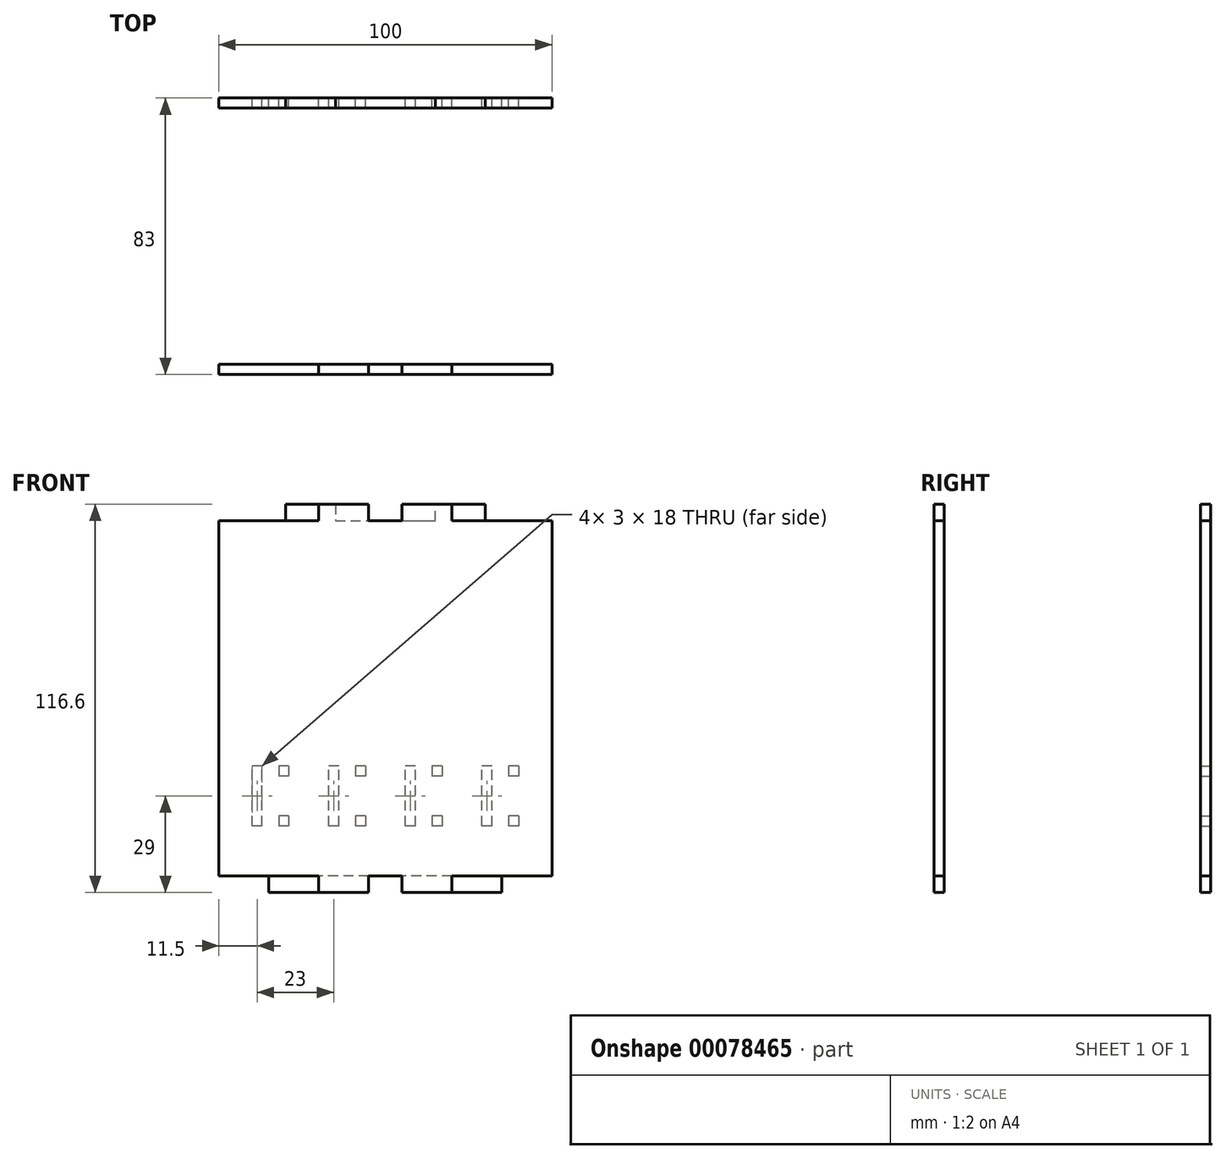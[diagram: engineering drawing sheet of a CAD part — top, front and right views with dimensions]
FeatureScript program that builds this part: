
annotation { "Feature Type Name" : "Feature", "Feature Type Description" : "" }
export const myFeature = defineFeature(function(context is Context, id is Id, definition is map)
    precondition{}
    {
        {
            var Q0;
            Q0=qCreatedBy(makeId("Front.planeOp"),FACE);
            var sketch = newSketch(context, id + "F0", { "sketchPlane" : qUnion([Q0])});
            skLineSegment(sketch, "E0", {"start": v(-50, 53.3) * mm, "end": v(-30, 53.3) * mm});
            skLineSegment(sketch, "E1", {"start": v(-30, 53.3) * mm, "end": v(-30, 58.3) * mm});
            skLineSegment(sketch, "E2", {"start": v(-30, 58.3) * mm, "end": v(-15, 58.3) * mm});
            skLineSegment(sketch, "E3", {"start": v(-15, 58.3) * mm, "end": v(-15, 53.3) * mm});
            skLineSegment(sketch, "E4", {"start": v(-15, 53.3) * mm, "end": v(15, 53.3) * mm});
            skLineSegment(sketch, "E5", {"start": v(15, 53.3) * mm, "end": v(15, 58.3) * mm});
            skLineSegment(sketch, "E6", {"start": v(15, 58.3) * mm, "end": v(30, 58.3) * mm});
            skLineSegment(sketch, "E7", {"start": v(30, 58.3) * mm, "end": v(30, 53.3) * mm});
            skLineSegment(sketch, "E8", {"start": v(30, 53.3) * mm, "end": v(50, 53.3) * mm});
            skLineSegment(sketch, "E9", {"start": v(50, 53.3) * mm, "end": v(50, -53.3) * mm});
            skLineSegment(sketch, "E10", {"start": v(50, -53.3) * mm, "end": v(35, -53.3) * mm});
            skLineSegment(sketch, "E11", {"start": v(35, -53.3) * mm, "end": v(35, -58.3) * mm});
            skLineSegment(sketch, "E12", {"start": v(35, -58.3) * mm, "end": v(20, -58.3) * mm});
            skLineSegment(sketch, "E13", {"start": v(20, -58.3) * mm, "end": v(20, -53.3) * mm});
            skLineSegment(sketch, "E14", {"start": v(20, -53.3) * mm, "end": v(-20, -53.3) * mm});
            skLineSegment(sketch, "E15", {"start": v(-20, -53.3) * mm, "end": v(-20, -58.3) * mm});
            skLineSegment(sketch, "E16", {"start": v(-20, -58.3) * mm, "end": v(-35, -58.3) * mm});
            skLineSegment(sketch, "E17", {"start": v(-35, -58.3) * mm, "end": v(-35, -53.3) * mm});
            skLineSegment(sketch, "E18", {"start": v(-35, -53.3) * mm, "end": v(-50, -53.3) * mm});
            skLineSegment(sketch, "E19", {"start": v(-50, -53.3) * mm, "end": v(-50, 53.3) * mm});
            skPoint(sketch, "E20", {"position": v(-50, 0) * mm});
            skLineSegment(sketch, "E21", {"start": v(-50, 0) * mm, "end": v(50, 0) * mm, "construction": true});
            skPoint(sketch, "E22", {"position": v(0, 0) * mm});
            skLineSegment(sketch, "E23.bottom", {"start": v(40, -20.3) * mm, "end": v(37, -20.3) * mm});
            skLineSegment(sketch, "E23.top", {"start": v(40, -23.3) * mm, "end": v(37, -23.3) * mm});
            skLineSegment(sketch, "E23.left", {"start": v(40, -20.3) * mm, "end": v(40, -23.3) * mm});
            skLineSegment(sketch, "E23.right", {"start": v(37, -20.3) * mm, "end": v(37, -23.3) * mm});
            skLineSegment(sketch, "E24.0.1.0", {"start": v(37, -35.3) * mm, "end": v(37, -38.3) * mm});
            skLineSegment(sketch, "E24.0.1.1", {"start": v(40, -35.3) * mm, "end": v(40, -38.3) * mm});
            skLineSegment(sketch, "E24.0.1.2", {"start": v(40, -38.3) * mm, "end": v(37, -38.3) * mm});
            skLineSegment(sketch, "E24.0.1.3", {"start": v(40, -35.3) * mm, "end": v(37, -35.3) * mm});
            skLineSegment(sketch, "E24.direction2", {"start": v(37, -23.3) * mm, "end": v(37, -38.3) * mm, "construction": true});
            skLineSegment(sketch, "E25.0.3.0", {"start": v(-194, -20.3) * mm, "end": v(-194, -23.3) * mm});
            skLineSegment(sketch, "E25.3.3.0", {"start": v(-191, -20.3) * mm, "end": v(-191, -23.3) * mm});
            skLineSegment(sketch, "E25.6.3.0", {"start": v(-191, -23.3) * mm, "end": v(-194, -23.3) * mm});
            skLineSegment(sketch, "E25.9.3.0", {"start": v(-191, -20.3) * mm, "end": v(-194, -20.3) * mm});
            skLineSegment(sketch, "E25.0.3.1", {"start": v(-194, -35.3) * mm, "end": v(-194, -38.3) * mm});
            skLineSegment(sketch, "E25.3.3.1", {"start": v(-191, -35.3) * mm, "end": v(-191, -38.3) * mm});
            skLineSegment(sketch, "E25.6.3.1", {"start": v(-191, -38.3) * mm, "end": v(-194, -38.3) * mm});
            skLineSegment(sketch, "E25.9.3.1", {"start": v(-191, -35.3) * mm, "end": v(-194, -35.3) * mm});
            skLineSegment(sketch, "E25.0.4.0", {"start": v(-271, -20.3) * mm, "end": v(-271, -23.3) * mm});
            skLineSegment(sketch, "E25.3.4.0", {"start": v(-268, -20.3) * mm, "end": v(-268, -23.3) * mm});
            skLineSegment(sketch, "E25.6.4.0", {"start": v(-268, -23.3) * mm, "end": v(-271, -23.3) * mm});
            skLineSegment(sketch, "E25.9.4.0", {"start": v(-268, -20.3) * mm, "end": v(-271, -20.3) * mm});
            skLineSegment(sketch, "E25.0.4.1", {"start": v(-271, -35.3) * mm, "end": v(-271, -38.3) * mm});
            skLineSegment(sketch, "E25.3.4.1", {"start": v(-268, -35.3) * mm, "end": v(-268, -38.3) * mm});
            skLineSegment(sketch, "E25.6.4.1", {"start": v(-268, -38.3) * mm, "end": v(-271, -38.3) * mm});
            skLineSegment(sketch, "E25.9.4.1", {"start": v(-268, -35.3) * mm, "end": v(-271, -35.3) * mm});
            skLineSegment(sketch, "E25.0.5.0", {"start": v(-348, -20.3) * mm, "end": v(-348, -23.3) * mm});
            skLineSegment(sketch, "E25.3.5.0", {"start": v(-345, -20.3) * mm, "end": v(-345, -23.3) * mm});
            skLineSegment(sketch, "E25.6.5.0", {"start": v(-345, -23.3) * mm, "end": v(-348, -23.3) * mm});
            skLineSegment(sketch, "E25.9.5.0", {"start": v(-345, -20.3) * mm, "end": v(-348, -20.3) * mm});
            skLineSegment(sketch, "E25.0.5.1", {"start": v(-348, -35.3) * mm, "end": v(-348, -38.3) * mm});
            skLineSegment(sketch, "E25.3.5.1", {"start": v(-345, -35.3) * mm, "end": v(-345, -38.3) * mm});
            skLineSegment(sketch, "E25.6.5.1", {"start": v(-345, -38.3) * mm, "end": v(-348, -38.3) * mm});
            skLineSegment(sketch, "E25.9.5.1", {"start": v(-345, -35.3) * mm, "end": v(-348, -35.3) * mm});
            skLineSegment(sketch, "E26.bottom", {"start": v(32, -38.3) * mm, "end": v(29, -38.3) * mm});
            skLineSegment(sketch, "E26.top", {"start": v(32, -20.3) * mm, "end": v(29, -20.3) * mm});
            skLineSegment(sketch, "E26.left", {"start": v(32, -38.3) * mm, "end": v(32, -20.3) * mm});
            skLineSegment(sketch, "E26.right", {"start": v(29, -38.3) * mm, "end": v(29, -20.3) * mm});
            skLineSegment(sketch, "E27.1.0.0", {"start": v(14, -23.3) * mm, "end": v(14, -38.3) * mm, "construction": true});
            skLineSegment(sketch, "E27.1.0.1", {"start": v(9, -38.3) * mm, "end": v(9, -20.3) * mm});
            skLineSegment(sketch, "E27.1.0.2", {"start": v(6, -38.3) * mm, "end": v(6, -20.3) * mm});
            skLineSegment(sketch, "E27.1.0.3", {"start": v(17, -35.3) * mm, "end": v(17, -38.3) * mm});
            skLineSegment(sketch, "E27.1.0.4", {"start": v(14, -35.3) * mm, "end": v(14, -38.3) * mm});
            skLineSegment(sketch, "E27.1.0.5", {"start": v(17, -35.3) * mm, "end": v(14, -35.3) * mm});
            skLineSegment(sketch, "E27.1.0.6", {"start": v(17, -20.3) * mm, "end": v(17, -23.3) * mm});
            skLineSegment(sketch, "E27.1.0.7", {"start": v(17, -38.3) * mm, "end": v(14, -38.3) * mm});
            skLineSegment(sketch, "E27.1.0.8", {"start": v(14, -20.3) * mm, "end": v(14, -23.3) * mm});
            skLineSegment(sketch, "E27.1.0.9", {"start": v(9, -20.3) * mm, "end": v(6, -20.3) * mm});
            skLineSegment(sketch, "E27.1.0.10", {"start": v(9, -38.3) * mm, "end": v(6, -38.3) * mm});
            skLineSegment(sketch, "E27.1.0.11", {"start": v(17, -23.3) * mm, "end": v(14, -23.3) * mm});
            skLineSegment(sketch, "E27.1.0.12", {"start": v(17, -20.3) * mm, "end": v(14, -20.3) * mm});
            skLineSegment(sketch, "E27.2.0.0", {"start": v(-9, -23.3) * mm, "end": v(-9, -38.3) * mm, "construction": true});
            skLineSegment(sketch, "E27.2.0.1", {"start": v(-14, -38.3) * mm, "end": v(-14, -20.3) * mm});
            skLineSegment(sketch, "E27.2.0.2", {"start": v(-17, -38.3) * mm, "end": v(-17, -20.3) * mm});
            skLineSegment(sketch, "E27.2.0.3", {"start": v(-6, -35.3) * mm, "end": v(-6, -38.3) * mm});
            skLineSegment(sketch, "E27.2.0.4", {"start": v(-9, -35.3) * mm, "end": v(-9, -38.3) * mm});
            skLineSegment(sketch, "E27.2.0.5", {"start": v(-6, -35.3) * mm, "end": v(-9, -35.3) * mm});
            skLineSegment(sketch, "E27.2.0.6", {"start": v(-6, -20.3) * mm, "end": v(-6, -23.3) * mm});
            skLineSegment(sketch, "E27.2.0.7", {"start": v(-6, -38.3) * mm, "end": v(-9, -38.3) * mm});
            skLineSegment(sketch, "E27.2.0.8", {"start": v(-9, -20.3) * mm, "end": v(-9, -23.3) * mm});
            skLineSegment(sketch, "E27.2.0.9", {"start": v(-14, -20.3) * mm, "end": v(-17, -20.3) * mm});
            skLineSegment(sketch, "E27.2.0.10", {"start": v(-14, -38.3) * mm, "end": v(-17, -38.3) * mm});
            skLineSegment(sketch, "E27.2.0.11", {"start": v(-6, -23.3) * mm, "end": v(-9, -23.3) * mm});
            skLineSegment(sketch, "E27.2.0.12", {"start": v(-6, -20.3) * mm, "end": v(-9, -20.3) * mm});
            skLineSegment(sketch, "E27.3.0.0", {"start": v(-32, -23.3) * mm, "end": v(-32, -38.3) * mm, "construction": true});
            skLineSegment(sketch, "E27.3.0.1", {"start": v(-37, -38.3) * mm, "end": v(-37, -20.3) * mm});
            skLineSegment(sketch, "E27.3.0.2", {"start": v(-40, -38.3) * mm, "end": v(-40, -20.3) * mm});
            skLineSegment(sketch, "E27.3.0.3", {"start": v(-29, -35.3) * mm, "end": v(-29, -38.3) * mm});
            skLineSegment(sketch, "E27.3.0.4", {"start": v(-32, -35.3) * mm, "end": v(-32, -38.3) * mm});
            skLineSegment(sketch, "E27.3.0.5", {"start": v(-29, -35.3) * mm, "end": v(-32, -35.3) * mm});
            skLineSegment(sketch, "E27.3.0.6", {"start": v(-29, -20.3) * mm, "end": v(-29, -23.3) * mm});
            skLineSegment(sketch, "E27.3.0.7", {"start": v(-29, -38.3) * mm, "end": v(-32, -38.3) * mm});
            skLineSegment(sketch, "E27.3.0.8", {"start": v(-32, -20.3) * mm, "end": v(-32, -23.3) * mm});
            skLineSegment(sketch, "E27.3.0.9", {"start": v(-37, -20.3) * mm, "end": v(-40, -20.3) * mm});
            skLineSegment(sketch, "E27.3.0.10", {"start": v(-37, -38.3) * mm, "end": v(-40, -38.3) * mm});
            skLineSegment(sketch, "E27.3.0.11", {"start": v(-29, -23.3) * mm, "end": v(-32, -23.3) * mm});
            skLineSegment(sketch, "E27.3.0.12", {"start": v(-29, -20.3) * mm, "end": v(-32, -20.3) * mm});
            skLineSegment(sketch, "E27.direction1", {"start": v(29, -38.3) * mm, "end": v(6, -38.3) * mm, "construction": true});
            skSolve(sketch);
        }
        {
            var Q0;
            Q0=makeQuery(id+"F0.imprint","IMPRINT",FACE,{"disambiguationData":[TD([[makeQuery(id+"F0.imprint","IMPRINT",EDGE,{"derivedFrom":sQuery(id+"F0.wireOp",EDGE,"E0")}),-1.0]])]});
            extrude(context, id + "F1", {"entities" : qUnion([Q0]), "depth" : 3 * mm});
        }
        {
            var Q0;
            Q0=qCreatedBy(makeId("Front.planeOp"),FACE);
            cPlane(context, id + "F2", {"entities" : qUnion([Q0]), "cplaneType" : CPlaneType.OFFSET, "offset" : 80 * mm, "width" : 150 * mm, "height" : 150 * mm});
        }
        {
            var Q0;
            Q0=qCreatedBy(id+"F2.planeOp",FACE);
            var sketch = newSketch(context, id + "F3", { "sketchPlane" : qUnion([Q0])});
            skLineSegment(sketch, "E28", {"start": v(-50, 53.3) * mm, "end": v(-20, 53.3) * mm});
            skLineSegment(sketch, "E29", {"start": v(-20, 53.3) * mm, "end": v(-20, 58.3) * mm});
            skLineSegment(sketch, "E30", {"start": v(-20, 58.3) * mm, "end": v(-5, 58.3) * mm});
            skLineSegment(sketch, "E31", {"start": v(-5, 58.3) * mm, "end": v(-5, 53.3) * mm});
            skLineSegment(sketch, "E32", {"start": v(-5, 53.3) * mm, "end": v(5, 53.3) * mm});
            skLineSegment(sketch, "E33", {"start": v(5, 53.3) * mm, "end": v(5, 58.3) * mm});
            skLineSegment(sketch, "E34", {"start": v(5, 58.3) * mm, "end": v(20, 58.3) * mm});
            skLineSegment(sketch, "E35", {"start": v(20, 58.3) * mm, "end": v(20, 53.3) * mm});
            skLineSegment(sketch, "E36", {"start": v(20, 53.3) * mm, "end": v(50, 53.3) * mm});
            skLineSegment(sketch, "E37", {"start": v(50, 53.3) * mm, "end": v(50, -53.3) * mm});
            skLineSegment(sketch, "E38", {"start": v(50, -53.3) * mm, "end": v(20, -53.3) * mm});
            skLineSegment(sketch, "E39", {"start": v(20, -53.3) * mm, "end": v(20, -58.3) * mm});
            skLineSegment(sketch, "E40", {"start": v(20, -58.3) * mm, "end": v(5, -58.3) * mm});
            skLineSegment(sketch, "E41", {"start": v(5, -58.3) * mm, "end": v(5, -53.3) * mm});
            skLineSegment(sketch, "E42", {"start": v(5, -53.3) * mm, "end": v(-5, -53.3) * mm});
            skLineSegment(sketch, "E43", {"start": v(-5, -53.3) * mm, "end": v(-5, -58.3) * mm});
            skLineSegment(sketch, "E44", {"start": v(-5, -58.3) * mm, "end": v(-20, -58.3) * mm});
            skLineSegment(sketch, "E45", {"start": v(-20, -58.3) * mm, "end": v(-20, -53.3) * mm});
            skLineSegment(sketch, "E46", {"start": v(-20, -53.3) * mm, "end": v(-50, -53.3) * mm});
            skLineSegment(sketch, "E47", {"start": v(-50, -53.3) * mm, "end": v(-50, 53.3) * mm});
            skPoint(sketch, "E48", {"position": v(-50, 0) * mm});
            skLineSegment(sketch, "E49", {"start": v(-50, 0) * mm, "end": v(50, 0) * mm, "construction": true});
            skPoint(sketch, "E50", {"position": v(0, 0) * mm});
            skSolve(sketch);
        }
        {
            var Q0;
            Q0=makeQuery(id+"F3.imprint","IMPRINT",FACE,{"disambiguationData":[TD([[makeQuery(id+"F3.imprint","IMPRINT",EDGE,{"derivedFrom":sQuery(id+"F3.wireOp",EDGE,"E28")}),-1.0]])]});
            extrude(context, id + "F4", {"entities" : qUnion([Q0]), "depth" : 3 * mm});
        }
    });
